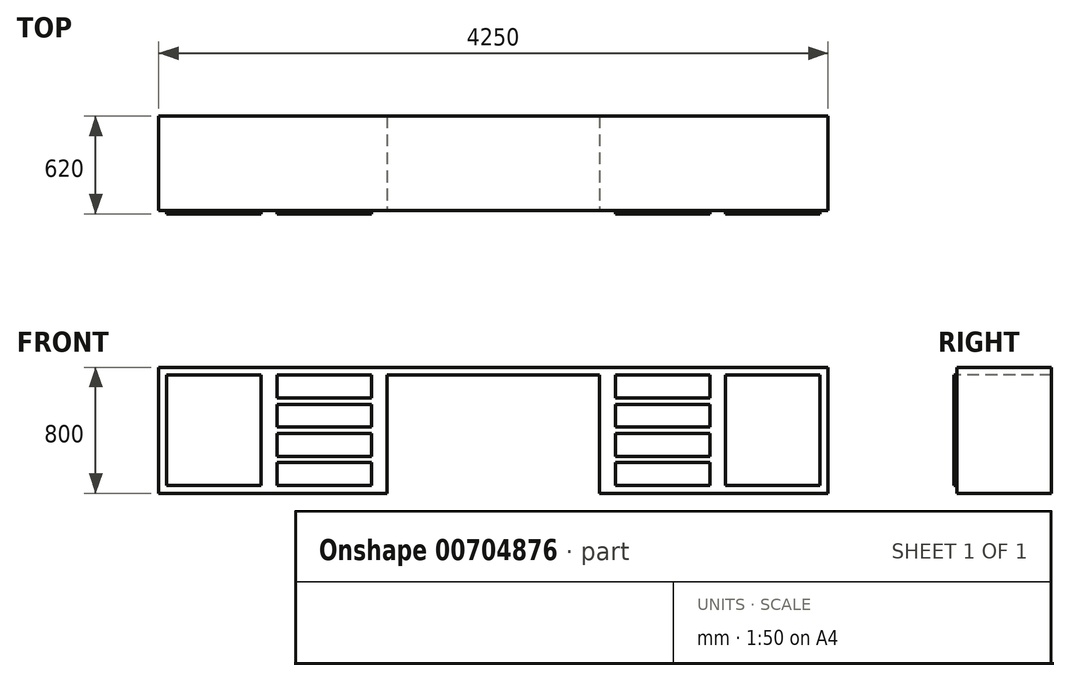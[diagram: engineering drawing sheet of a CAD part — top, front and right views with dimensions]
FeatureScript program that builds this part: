
annotation { "Feature Type Name" : "Feature", "Feature Type Description" : "" }
export const myFeature = defineFeature(function(context is Context, id is Id, definition is map)
    precondition{}
    {
        {
            var Q0;
            Q0=qCreatedBy(makeId("Top.planeOp"),FACE);
            var sketch = newSketch(context, id + "F0", { "sketchPlane" : qUnion([Q0])});
            skLineSegment(sketch, "E0.bottom", {"start": v(2125, -300) * mm, "end": v(-2125, -300) * mm});
            skLineSegment(sketch, "E0.top", {"start": v(2125, 300) * mm, "end": v(-2125, 300) * mm});
            skLineSegment(sketch, "E0.left", {"start": v(2125, -300) * mm, "end": v(2125, 300) * mm});
            skLineSegment(sketch, "E0.right", {"start": v(-2125, -300) * mm, "end": v(-2125, 300) * mm});
            skPoint(sketch, "E0.middle", {"position": v(0, 0) * mm});
            skSolve(sketch);
        }
        {
            var Q0;
            Q0=makeQuery(id+"F0.imprint","IMPRINT",FACE,{"disambiguationData":[TD([[makeQuery(id+"F0.imprint","IMPRINT",EDGE,{"derivedFrom":sQuery(id+"F0.wireOp",EDGE,"E0.bottom")}),-1.0]])]});
            extrude(context, id + "F1", {"entities" : qUnion([Q0]), "depth" : 800 * mm, "offsetDistance" : 25 * mm});
        }
        {
            var Q0;
            Q0=makeQuery(id+"F1.opExtrude","SWEPT_FACE",FACE,{"disambiguationData":[OSD([sQuery(id+"F0.wireOp",EDGE,"E0.bottom")])]});
            var sketch = newSketch(context, id + "F2", { "sketchPlane" : qUnion([Q0])});
            skLineSegment(sketch, "E1.bottom", {"start": v(-2075, 750) * mm, "end": v(-1475, 750) * mm});
            skLineSegment(sketch, "E1.top", {"start": v(-2075, 50) * mm, "end": v(-1475, 50) * mm});
            skLineSegment(sketch, "E1.left", {"start": v(-2075, 750) * mm, "end": v(-2075, 50) * mm});
            skLineSegment(sketch, "E1.right", {"start": v(-1475, 750) * mm, "end": v(-1475, 50) * mm});
            skLineSegment(sketch, "E2", {"start": v(0, 0) * mm, "end": v(0, 911.39) * mm, "construction": true});
            skLineSegment(sketch, "E3.MirrorCS", {"start": v(1475, 750) * mm, "end": v(1475, 50) * mm});
            skLineSegment(sketch, "E4.MirrorCS", {"start": v(2075, 50) * mm, "end": v(1475, 50) * mm});
            skLineSegment(sketch, "E5.MirrorCS", {"start": v(2075, 750) * mm, "end": v(2075, 50) * mm});
            skLineSegment(sketch, "E6.MirrorCS", {"start": v(2075, 750) * mm, "end": v(1475, 750) * mm});
            skLineSegment(sketch, "E7", {"start": v(-675, 0) * mm, "end": v(-675, 750) * mm});
            skLineSegment(sketch, "E8", {"start": v(-675, 750) * mm, "end": v(675, 750) * mm});
            skLineSegment(sketch, "E9", {"start": v(675, 750) * mm, "end": v(675, 0) * mm});
            skLineSegment(sketch, "E10.bottom", {"start": v(-1375, 750) * mm, "end": v(-775, 750) * mm});
            skLineSegment(sketch, "E10.top", {"start": v(-1375, 605) * mm, "end": v(-775, 605) * mm});
            skLineSegment(sketch, "E10.left", {"start": v(-1375, 750) * mm, "end": v(-1375, 605) * mm});
            skLineSegment(sketch, "E10.right", {"start": v(-775, 750) * mm, "end": v(-775, 605) * mm});
            skLineSegment(sketch, "E11.bottom", {"start": v(-1375, 565) * mm, "end": v(-775, 565) * mm});
            skLineSegment(sketch, "E11.top", {"start": v(-1375, 420) * mm, "end": v(-775, 420) * mm});
            skLineSegment(sketch, "E11.left", {"start": v(-1375, 565) * mm, "end": v(-1375, 420) * mm});
            skLineSegment(sketch, "E11.right", {"start": v(-775, 565) * mm, "end": v(-775, 420) * mm});
            skLineSegment(sketch, "E12.bottom", {"start": v(-1375, 380) * mm, "end": v(-775, 380) * mm});
            skLineSegment(sketch, "E12.top", {"start": v(-1375, 235) * mm, "end": v(-775, 235) * mm});
            skLineSegment(sketch, "E12.left", {"start": v(-1375, 380) * mm, "end": v(-1375, 235) * mm});
            skLineSegment(sketch, "E12.right", {"start": v(-775, 380) * mm, "end": v(-775, 235) * mm});
            skLineSegment(sketch, "E13.bottom", {"start": v(-1375, 195) * mm, "end": v(-775, 195) * mm});
            skLineSegment(sketch, "E13.top", {"start": v(-1375, 50) * mm, "end": v(-775, 50) * mm});
            skLineSegment(sketch, "E13.left", {"start": v(-1375, 195) * mm, "end": v(-1375, 50) * mm});
            skLineSegment(sketch, "E13.right", {"start": v(-775, 195) * mm, "end": v(-775, 50) * mm});
            skLineSegment(sketch, "E14.MirrorCS", {"start": v(1375, 750) * mm, "end": v(775, 750) * mm});
            skLineSegment(sketch, "E15.MirrorCS", {"start": v(1375, 605) * mm, "end": v(775, 605) * mm});
            skLineSegment(sketch, "E16.MirrorCS", {"start": v(1375, 565) * mm, "end": v(775, 565) * mm});
            skLineSegment(sketch, "E17.MirrorCS", {"start": v(1375, 420) * mm, "end": v(775, 420) * mm});
            skLineSegment(sketch, "E18.MirrorCS", {"start": v(1375, 380) * mm, "end": v(775, 380) * mm});
            skLineSegment(sketch, "E19.MirrorCS", {"start": v(1375, 235) * mm, "end": v(775, 235) * mm});
            skLineSegment(sketch, "E20.MirrorCS", {"start": v(1375, 195) * mm, "end": v(775, 195) * mm});
            skLineSegment(sketch, "E21.MirrorCS", {"start": v(1375, 50) * mm, "end": v(775, 50) * mm});
            skLineSegment(sketch, "E22.MirrorCS", {"start": v(775, 195) * mm, "end": v(775, 50) * mm});
            skLineSegment(sketch, "E23.MirrorCS", {"start": v(775, 380) * mm, "end": v(775, 235) * mm});
            skLineSegment(sketch, "E24.MirrorCS", {"start": v(775, 565) * mm, "end": v(775, 420) * mm});
            skLineSegment(sketch, "E25.MirrorCS", {"start": v(775, 750) * mm, "end": v(775, 605) * mm});
            skLineSegment(sketch, "E26.MirrorCS", {"start": v(1375, 750) * mm, "end": v(1375, 605) * mm});
            skLineSegment(sketch, "E27.MirrorCS", {"start": v(1375, 565) * mm, "end": v(1375, 420) * mm});
            skLineSegment(sketch, "E28.MirrorCS", {"start": v(1375, 380) * mm, "end": v(1375, 235) * mm});
            skLineSegment(sketch, "E29.MirrorCS", {"start": v(1375, 195) * mm, "end": v(1375, 50) * mm});
            skSolve(sketch);
        }
        {
            var Q0;
            Q0=makeQuery(id+"F2.imprint","IMPRINT",FACE,{"disambiguationData":[TD([[makeQuery(id+"F2.imprint","IMPRINT",EDGE,{"derivedFrom":sQuery(id+"F2.wireOp",EDGE,"E1.bottom")}),-1.0]])]});
            var Q1;
            Q1=makeQuery(id+"F2.imprint","IMPRINT",FACE,{"disambiguationData":[TD([[makeQuery(id+"F2.imprint","IMPRINT",EDGE,{"derivedFrom":sQuery(id+"F2.wireOp",EDGE,"E10.bottom")}),-1.0]])]});
            var Q2;
            Q2=makeQuery(id+"F2.imprint","IMPRINT",FACE,{"disambiguationData":[TD([[makeQuery(id+"F2.imprint","IMPRINT",EDGE,{"derivedFrom":sQuery(id+"F2.wireOp",EDGE,"E11.bottom")}),-1.0]])]});
            var Q3;
            Q3=makeQuery(id+"F2.imprint","IMPRINT",FACE,{"disambiguationData":[TD([[makeQuery(id+"F2.imprint","IMPRINT",EDGE,{"derivedFrom":sQuery(id+"F2.wireOp",EDGE,"E12.bottom")}),-1.0]])]});
            var Q4;
            Q4=makeQuery(id+"F2.imprint","IMPRINT",FACE,{"disambiguationData":[TD([[makeQuery(id+"F2.imprint","IMPRINT",EDGE,{"derivedFrom":sQuery(id+"F2.wireOp",EDGE,"E13.bottom")}),-1.0]])]});
            var Q5;
            Q5=makeQuery(id+"F2.imprint","IMPRINT",FACE,{"disambiguationData":[TD([[makeQuery(id+"F2.imprint","IMPRINT",EDGE,{"derivedFrom":sQuery(id+"F2.wireOp",EDGE,"E14.MirrorCS")}),1.0]])]});
            var Q6;
            Q6=makeQuery(id+"F2.imprint","IMPRINT",FACE,{"disambiguationData":[TD([[makeQuery(id+"F2.imprint","IMPRINT",EDGE,{"derivedFrom":sQuery(id+"F2.wireOp",EDGE,"E16.MirrorCS")}),1.0]])]});
            var Q7;
            Q7=makeQuery(id+"F2.imprint","IMPRINT",FACE,{"disambiguationData":[TD([[makeQuery(id+"F2.imprint","IMPRINT",EDGE,{"derivedFrom":sQuery(id+"F2.wireOp",EDGE,"E18.MirrorCS")}),1.0]])]});
            var Q8;
            Q8=makeQuery(id+"F2.imprint","IMPRINT",FACE,{"disambiguationData":[TD([[makeQuery(id+"F2.imprint","IMPRINT",EDGE,{"derivedFrom":sQuery(id+"F2.wireOp",EDGE,"E20.MirrorCS")}),1.0]])]});
            var Q9;
            Q9=makeQuery(id+"F2.imprint","IMPRINT",FACE,{"disambiguationData":[TD([[makeQuery(id+"F2.imprint","IMPRINT",EDGE,{"derivedFrom":sQuery(id+"F2.wireOp",EDGE,"E3.MirrorCS")}),1.0]])]});
            extrude(context, id + "F3", {"entities" : qUnion([Q0, Q1, Q2, Q3, Q4, Q5, Q6, Q7, Q8, Q9]), "operationType" : NewBodyOperationType.ADD, "depth" : 20 * mm, "offsetDistance" : 25 * mm});
        }
        {
            var Q0;
            {var subQ0=sQuery(id+"F2.wireOp",EDGE,"E7");Q0=makeQuery(id+"F2.imprint","IMPRINT",FACE,{"disambiguationData":[TD([[makeQuery(id+"F2.imprint","IMPRINT",EDGE,{"derivedFrom":subQ0}),-1.0]])]});}
            extrude(context, id + "F4", {"entities" : qUnion([Q0]), "operationType" : NewBodyOperationType.REMOVE, "oppositeDirection" : true, "depth" : 700 * mm, "offsetDistance" : 25 * mm});
        }
    });
